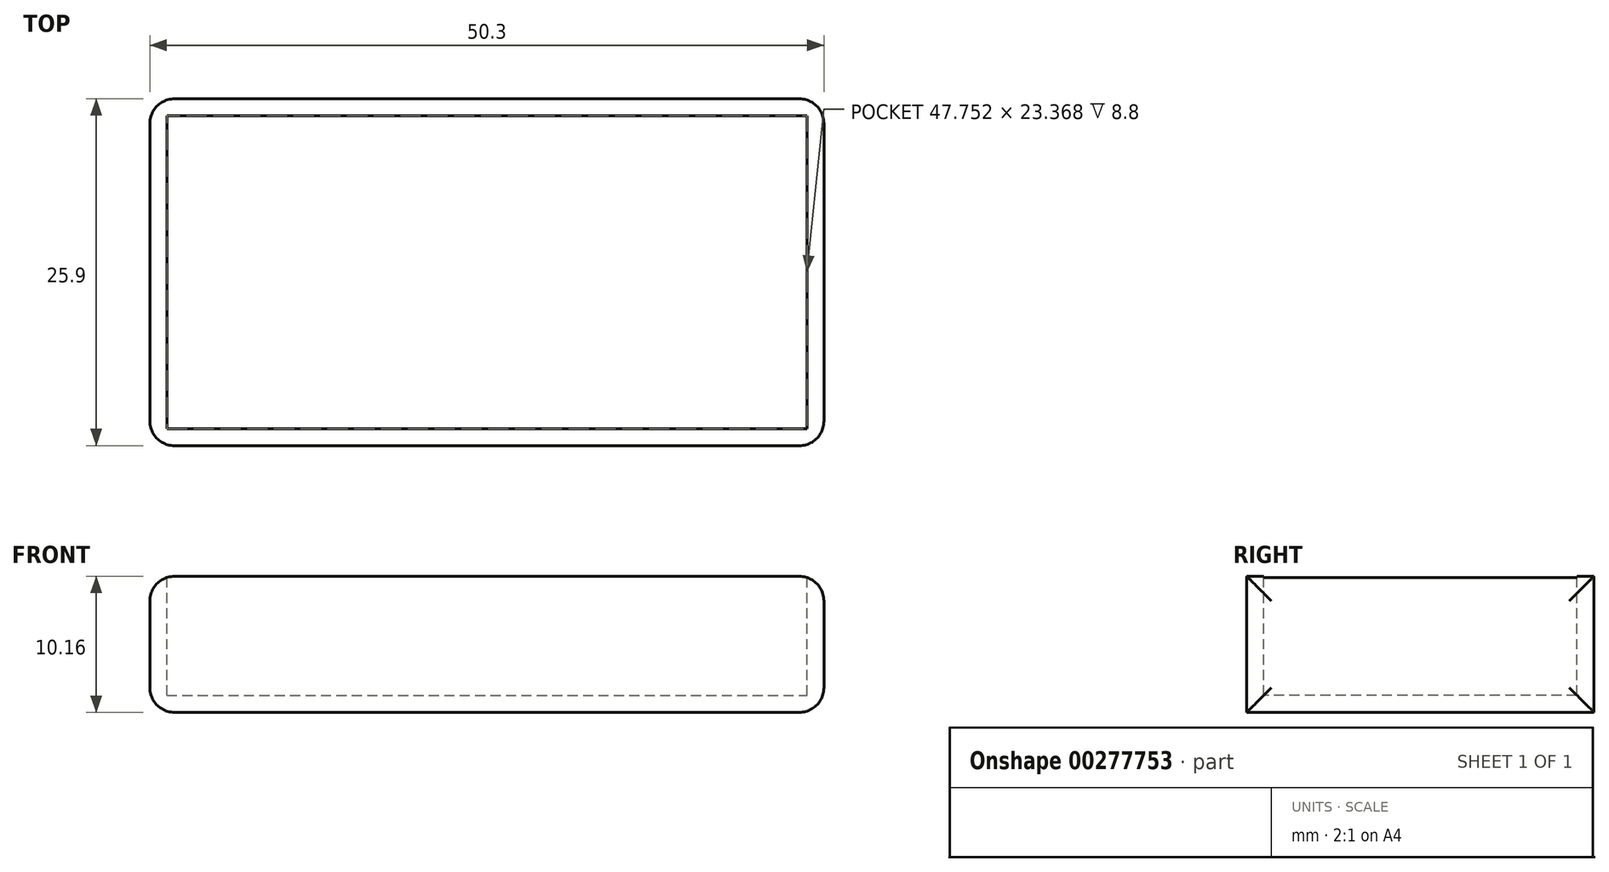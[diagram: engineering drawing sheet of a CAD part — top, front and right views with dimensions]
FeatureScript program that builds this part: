
annotation { "Feature Type Name" : "Feature", "Feature Type Description" : "" }
export const myFeature = defineFeature(function(context is Context, id is Id, definition is map)
    precondition{}
    {
        {
            var Q0;
            Q0=qCreatedBy(makeId("Top.planeOp"),FACE);
            var sketch = newSketch(context, id + "F0", { "sketchPlane" : qUnion([Q0])});
            skLineSegment(sketch, "E0.bottom", {"start": v(-25.15, 12.95) * mm, "end": v(25.15, 12.95) * mm});
            skLineSegment(sketch, "E0.top", {"start": v(-25.15, -12.95) * mm, "end": v(25.15, -12.95) * mm});
            skLineSegment(sketch, "E0.left", {"start": v(-25.15, 12.95) * mm, "end": v(-25.15, -12.95) * mm});
            skLineSegment(sketch, "E0.right", {"start": v(25.15, 12.95) * mm, "end": v(25.15, -12.95) * mm});
            skPoint(sketch, "E0.middle", {"position": v(0, 0) * mm});
            skSolve(sketch);
        }
        {
            var Q0;
            Q0 = qSketchRegion(id + "F0", true);
            var Q1;
            Q1 = qSketchRegion(id + "F2", true);
            extrude(context, id + "F1", {"entities" : qUnion([Q0, Q1]), "depth" : 10.16 * mm});
        }
        {
            var Q0;
            Q0=makeQuery(id+"F1.opExtrude","CAP_FACE",FACE,{"disambiguationData":[OSD([sQuery(id+"F0.wireOp",EDGE,"E0.bottom"),sQuery(id+"F0.wireOp",EDGE,"E0.top"),sQuery(id+"F0.wireOp",EDGE,"E0.left"),sQuery(id+"F0.wireOp",EDGE,"E0.right")])],"isStart":false});
            var sketch = newSketch(context, id + "F2", { "sketchPlane" : qUnion([Q0])});
            skLineSegment(sketch, "E1.bottom", {"start": v(-23.88, 11.68) * mm, "end": v(23.88, 11.68) * mm});
            skLineSegment(sketch, "E1.top", {"start": v(-23.88, -11.68) * mm, "end": v(23.88, -11.68) * mm});
            skLineSegment(sketch, "E1.left", {"start": v(-23.88, 11.68) * mm, "end": v(-23.88, -11.68) * mm});
            skLineSegment(sketch, "E1.right", {"start": v(23.88, 11.68) * mm, "end": v(23.88, -11.68) * mm});
            skPoint(sketch, "E1.middle", {"position": v(0, 0) * mm});
            skSolve(sketch);
        }
        {
            var Q0;
            Q0 = qSketchRegion(id + "F2", true);
            extrude(context, id + "F3", {"entities" : qUnion([Q0]), "operationType" : NewBodyOperationType.REMOVE, "oppositeDirection" : true, "depth" : 8.9 * mm});
        }
        {
            var Q0;
            Q0=makeQuery(id+"F1.opExtrude","SWEPT_FACE",FACE,{"disambiguationData":[OSD([sQuery(id+"F0.wireOp",EDGE,"E0.left")])]});
            fillet(context, id + "F4", {"entities" : qUnion([Q0]), "radius" : 1.84 * mm, "tangentPropagation" : true, "allowEdgeOverflow" : false});
        }
        {
            var Q0;
            Q0=makeQuery(id+"F1.opExtrude","SWEPT_FACE",FACE,{"disambiguationData":[OSD([sQuery(id+"F0.wireOp",EDGE,"E0.right")])]});
            fillet(context, id + "F5", {"entities" : qUnion([Q0]), "radius" : 1.84 * mm, "tangentPropagation" : true, "allowEdgeOverflow" : false});
        }
    });
